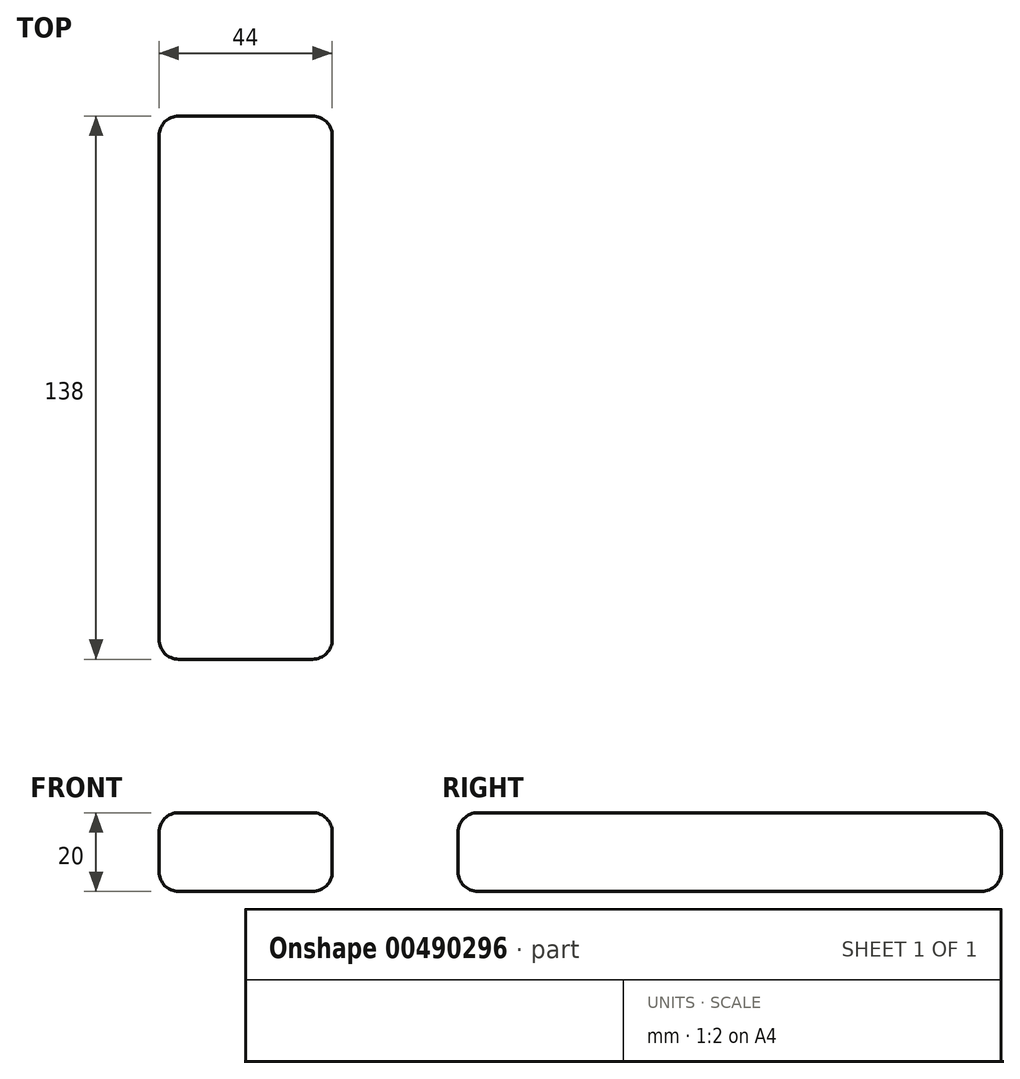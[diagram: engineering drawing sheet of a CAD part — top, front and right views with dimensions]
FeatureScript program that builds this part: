
annotation { "Feature Type Name" : "Feature", "Feature Type Description" : "" }
export const myFeature = defineFeature(function(context is Context, id is Id, definition is map)
    precondition{}
    {
        {
            var Q0;
            Q0=qCreatedBy(makeId("Top.planeOp"),FACE);
            var sketch = newSketch(context, id + "F0", { "sketchPlane" : qUnion([Q0])});
            skLineSegment(sketch, "E0.bottom", {"start": v(22, -69) * mm, "end": v(-22, -69) * mm});
            skLineSegment(sketch, "E0.top", {"start": v(22, 69) * mm, "end": v(-22, 69) * mm});
            skLineSegment(sketch, "E0.left", {"start": v(22, -69) * mm, "end": v(22, 69) * mm});
            skLineSegment(sketch, "E0.right", {"start": v(-22, -69) * mm, "end": v(-22, 69) * mm});
            skPoint(sketch, "E0.middle", {"position": v(0, 0) * mm});
            skSolve(sketch);
        }
        {
            var Q0;
            Q0 = qSketchRegion(id + "F0", true);
            extrude(context, id + "F1", {"entities" : qUnion([Q0]), "depth" : 20 * mm, "offsetDistance" : 25 * mm});
        }
        {
            var Q0;
            Q0=makeQuery(id+"F1.opExtrude","CAP_EDGE",EDGE,{"disambiguationData":[OSD([sQuery(id+"F0.wireOp",EDGE,"E0.right")])],"isStart":true});
            var Q1;
            Q1=makeQuery(id+"F1.opExtrude","CAP_EDGE",EDGE,{"disambiguationData":[OSD([sQuery(id+"F0.wireOp",EDGE,"E0.right")])],"isStart":false});
            var Q2;
            Q2=makeQuery(id+"F1.opExtrude","CAP_EDGE",EDGE,{"disambiguationData":[OSD([sQuery(id+"F0.wireOp",EDGE,"E0.left")])],"isStart":false});
            var Q3;
            Q3=makeQuery(id+"F1.opExtrude","CAP_EDGE",EDGE,{"disambiguationData":[OSD([sQuery(id+"F0.wireOp",EDGE,"E0.left")])],"isStart":true});
            var Q4;
            Q4=makeQuery(id+"F1.opExtrude","SWEPT_FACE",FACE,{"disambiguationData":[OSD([sQuery(id+"F0.wireOp",EDGE,"E0.top")])]});
            var Q5;
            Q5=makeQuery(id+"F1.opExtrude","SWEPT_FACE",FACE,{"disambiguationData":[OSD([sQuery(id+"F0.wireOp",EDGE,"E0.bottom")])]});
            fillet(context, id + "F2", {"entities" : qUnion([Q0, Q1, Q2, Q3, Q4, Q5]), "radius" : 5 * mm, "tangentPropagation" : true, "allowEdgeOverflow" : false});
        }
    });
